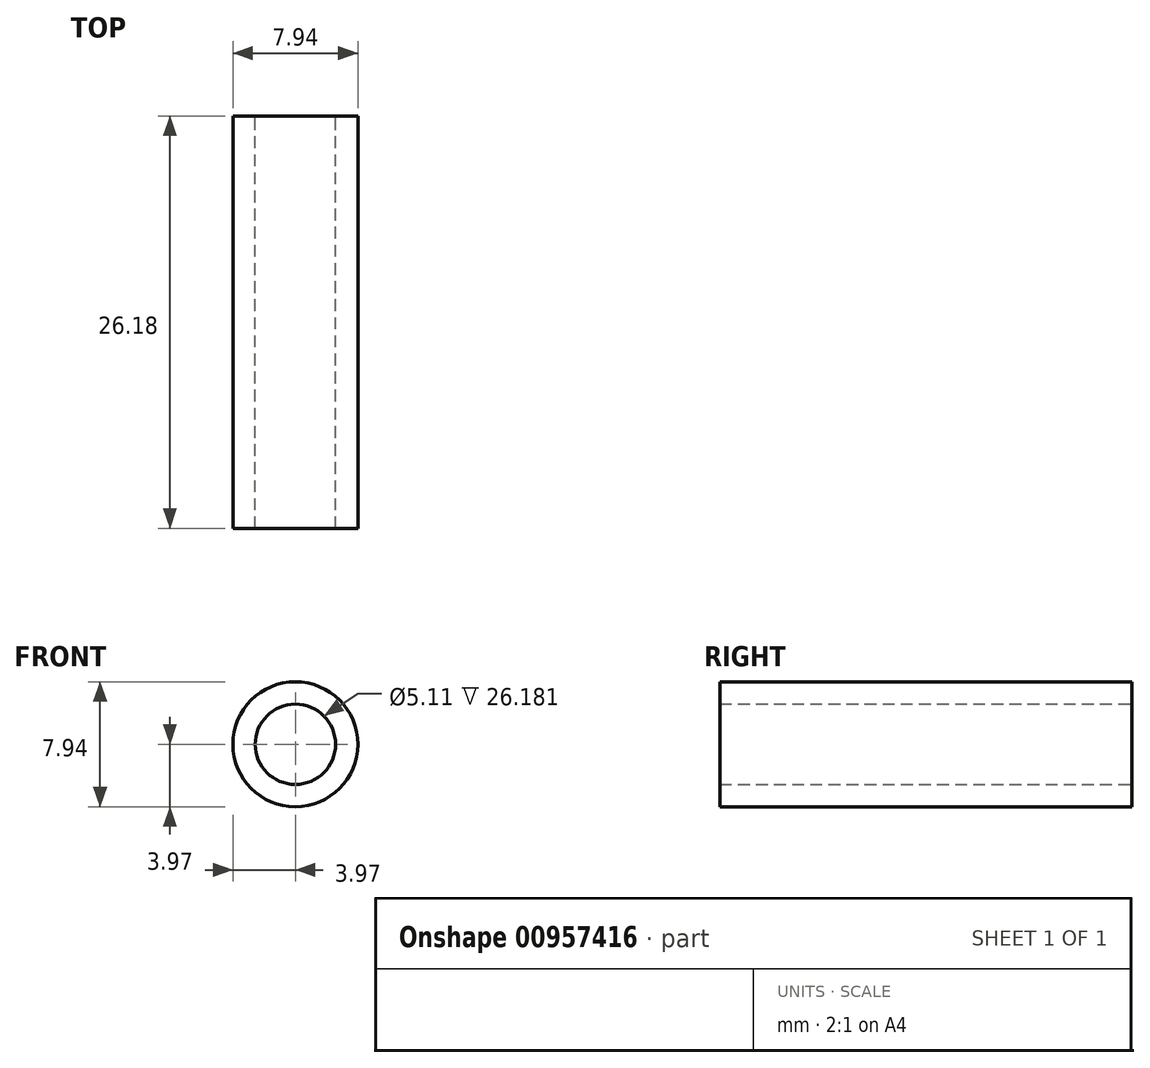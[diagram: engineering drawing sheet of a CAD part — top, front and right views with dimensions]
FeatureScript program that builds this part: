
annotation { "Feature Type Name" : "Feature", "Feature Type Description" : "" }
export const myFeature = defineFeature(function(context is Context, id is Id, definition is map)
    precondition{}
    {
        {
            var Q0;
            Q0=qCreatedBy(makeId("Front.planeOp"),FACE);
            var sketch = newSketch(context, id + "F0", { "sketchPlane" : qUnion([Q0])});
            skCircle(sketch, "E0", {"center": v(0, 0) * mm, "radius": 3.97 * mm});
            skCircle(sketch, "E1", {"center": v(0, 0) * mm, "radius": 2.55 * mm});
            skSolve(sketch);
        }
        {
            var Q0;
            Q0=qSketchRegion(id+"F0",true);
            extrude(context, id + "F1", {"entities" : qUnion([Q0]), "depth" : 26.18 * mm, "offsetDistance" : 25.4 * mm});
        }
    });
